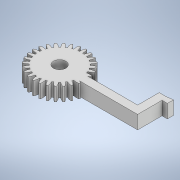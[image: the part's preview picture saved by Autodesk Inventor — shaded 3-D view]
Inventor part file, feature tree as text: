
AUTODESK INVENTOR PART (.ipt)
format: ipt  version: 2022 (Build 260153000, 153)  size: 403,456 bytes
history: native  units: in
note: dims shown in document units (in); Inventor stores cm internally (conversion verified against a paired STEP export)
features: extrude x12, sketch x12, pattern_circular x1
ambient origin geometry x8: Origin, YZ Plane, XZ Plane, XY Plane, X Axis, Y Axis, Z Axis, Center Point
bodies: Solid1 (feature_tree)
feature tree (25):
  extrude  "Extrusion1"  Depth=0.1575in
  pattern_circular  "Circular Pattern1"  Count=28 Angle=360.0deg
  extrude  "Extrusion6"  Depth=0.1969in
  extrude  "Extrusion7"  Depth=1.1811in
  extrude  "Extrusion8"  Depth=0.748in
  extrude  "Extrusion9"  Depth=0.1969in
  extrude  "Extrusion10"  Depth=0.1969in
  extrude  "Extrusion11"  Depth=0.1969in
  extrude  "Extrusion12"  Depth=0.1969in
  extrude  "Extrusion13"  Depth=0.1969in
  extrude  "Extrusion14"  Depth=0.1969in
  extrude  "Extrusion15"  Depth=0.1969in
  extrude  "Extrusion16"  Depth=0.1181in
  sketch  "Sketch1"  dims[d0=0.6299in d1=0.1575in]
  sketch  "Sketch8"  dims[d2=0.0098in]
  sketch  "Sketch9"  dims[d3=0.0098in]
  sketch  "Sketch10"  dims[d4=0.0236in]
  sketch  "Sketch11"  dims[d7=0.0472in]
  sketch  "Sketch12"  dims[d8=0.1772in]
  sketch  "Sketch13"  dims[d10=0.0787in]
  sketch  "Sketch14"  dims[d11=0.1969in d12=0.0in d13=11.0236in d14=360.0deg]
  sketch  "Sketch15"  dims[d49=0.1969in d50=0.1575in]
  sketch  "Sketch16"  dims[d51=0.5438in d52=0.0in d53=1.1811in]
  sketch  "Sketch17"  dims[d54=0.7087in d55=0.748in]
  sketch  "Sketch18"  dims[d56=0.748in d57=0.1969in d58=0.9843in d59=0.0591in d60=0.0591in d61=0.0591in d62=0.3543in d63=0.0591in d64=0.1181in d65=0.1969in d66=0.0197in d67=0.0197in d68=0.0197in d69=0.1969in d70=0.0in d71=1.1811in d72=0.3543in d73=0.1181in d74=0.1181in d75=0.3543in d76=0.1181in d77=0.1969in d78=0.0197in d79=0.1969in d80=0.0197in d81=0.0197in d82=0.1969in d83=0.0in d84=0.1811in d85=0.1969in d86=0.0in d87=0.4813in d88=0.0in d89=0.1181in d90=0.3543in d91=0.9843in d92=1.2205in d93=0.1181in d94=0.1181in d95=0.0787in d96=0.1969in d97=0.0in d98=0.0787in d99=0.0394in d100=0.4188in d101=0.0in d102=0.0394in d103=0.0394in d104=0.3937in d105=0.0in d106=0.1181in d107=0.0591in d108=0.6063in d109=0.0in d110=0.1181in d111=0.2756in d112=0.9843in d113=1.2205in d114=0.0787in d115=0.0787in d116=0.0394in d117=0.1969in d118=0.0in d119=0.3031in d120=0.0in]
